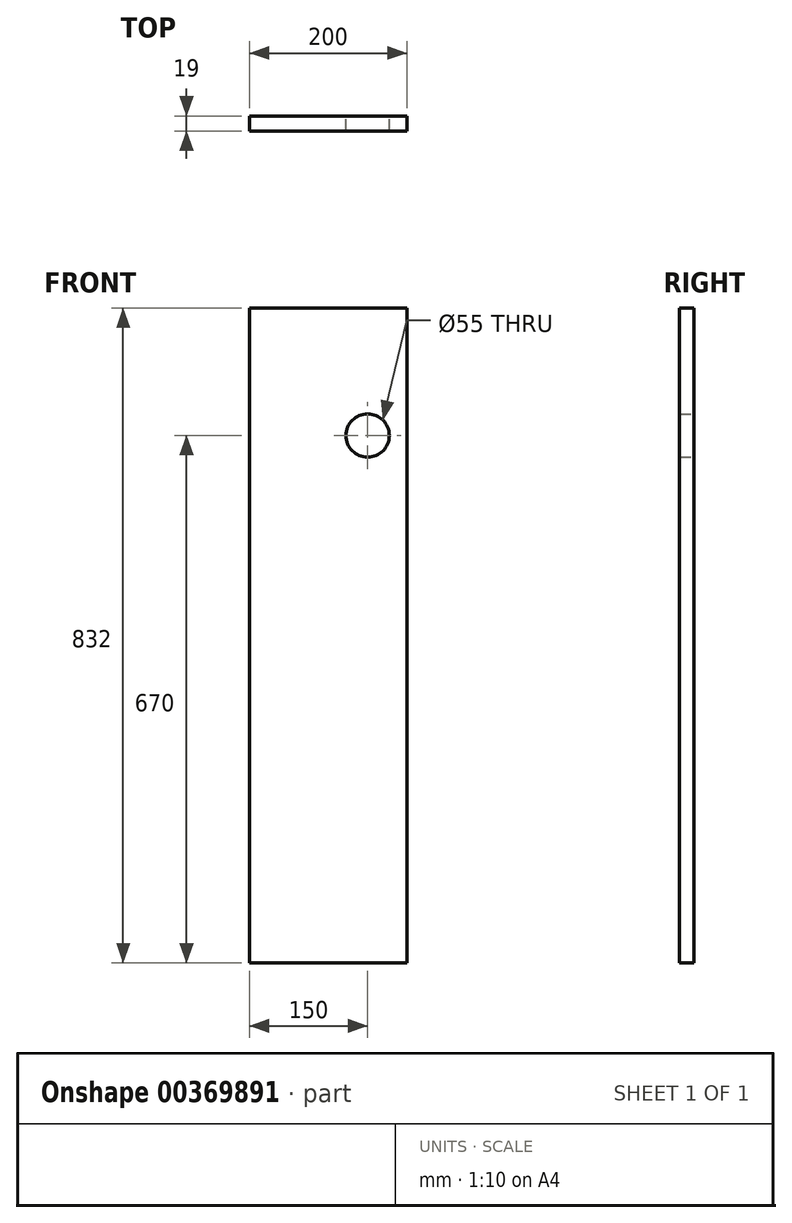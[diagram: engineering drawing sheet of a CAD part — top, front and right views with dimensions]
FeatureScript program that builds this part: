
annotation { "Feature Type Name" : "Feature", "Feature Type Description" : "" }
export const myFeature = defineFeature(function(context is Context, id is Id, definition is map)
    precondition{}
    {
        {
            var Q0;
            Q0=qCreatedBy(makeId("Front.planeOp"),FACE);
            var sketch = newSketch(context, id + "F0", { "sketchPlane" : qUnion([Q0])});
            skLineSegment(sketch, "E0.bottom", {"start": v(200, 832) * mm, "end": v(0, 832) * mm});
            skLineSegment(sketch, "E0.top", {"start": v(200, 0) * mm, "end": v(0, 0) * mm});
            skLineSegment(sketch, "E0.left", {"start": v(200, 832) * mm, "end": v(200, 0) * mm});
            skLineSegment(sketch, "E0.right", {"start": v(0, 832) * mm, "end": v(0, 0) * mm});
            skCircle(sketch, "E1", {"center": v(150, 670) * mm, "radius": 27.5 * mm});
            skSolve(sketch);
        }
        {
            var Q0;
            Q0=makeQuery(id+"F0.imprint","IMPRINT",FACE,{"disambiguationData":[TD([[makeQuery(id+"F0.imprint","IMPRINT",EDGE,{"derivedFrom":sQuery(id+"F0.wireOp",EDGE,"E0.bottom")}),1.0]])]});
            extrude(context, id + "F1", {"entities" : qUnion([Q0]), "depth" : 19 * mm});
        }
    });
